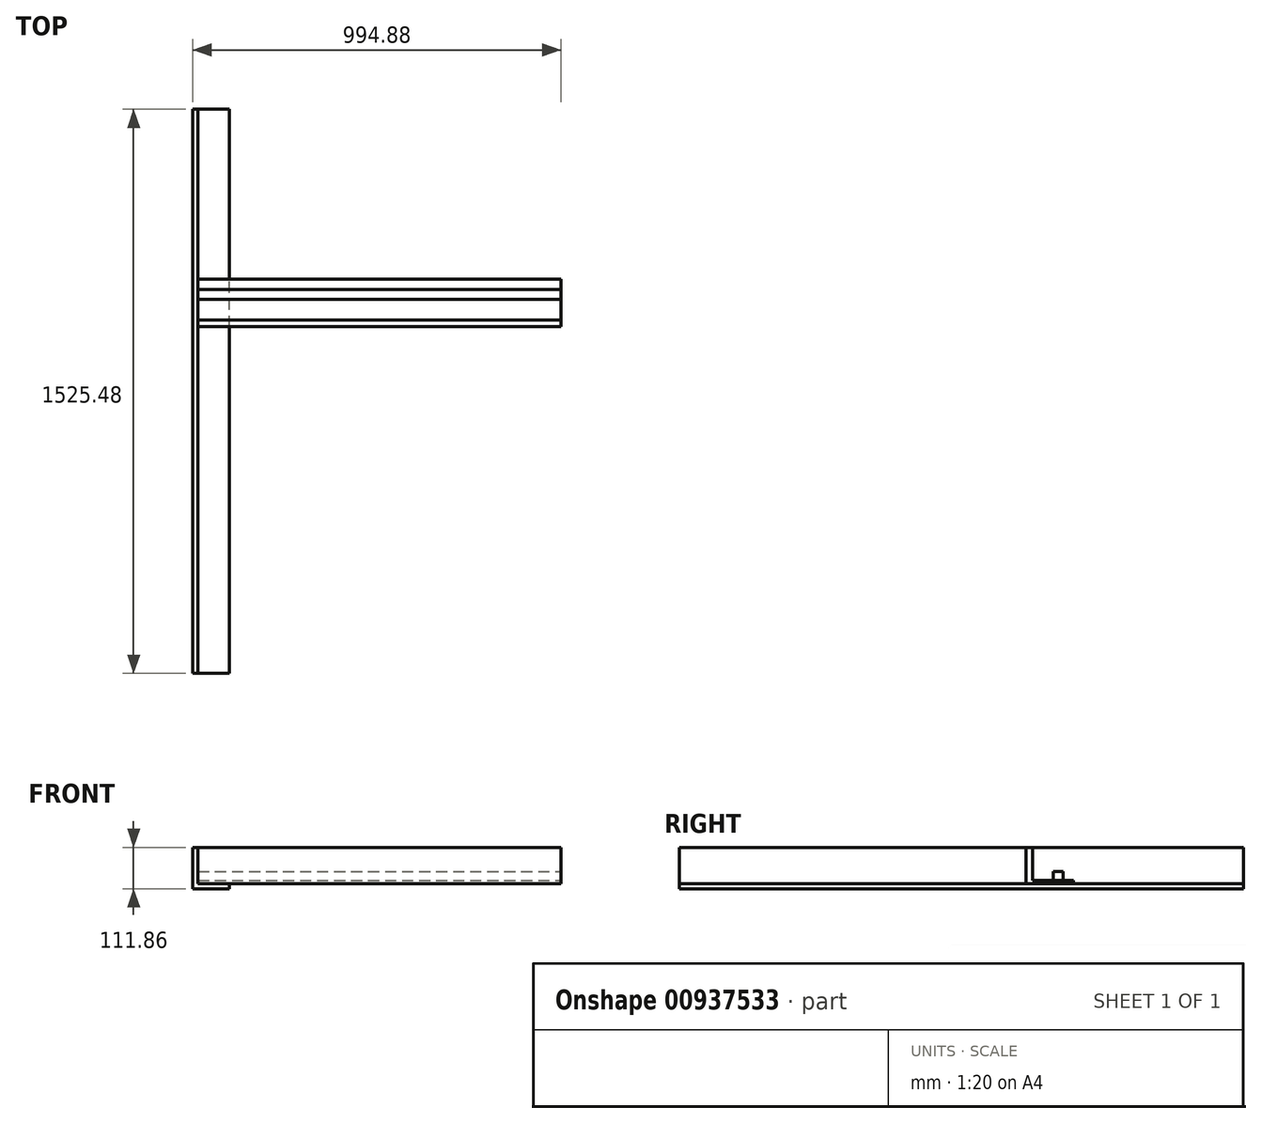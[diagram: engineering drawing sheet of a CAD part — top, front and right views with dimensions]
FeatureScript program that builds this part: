
annotation { "Feature Type Name" : "Feature", "Feature Type Description" : "" }
export const myFeature = defineFeature(function(context is Context, id is Id, definition is map)
    precondition{}
    {
        {
            var Q0;
            Q0=qCreatedBy(makeId("Front.planeOp"),FACE);
            var sketch = newSketch(context, id + "F0", { "sketchPlane" : qUnion([Q0])});
            skLineSegment(sketch, "E0", {"start": v(-31.08, 59.94) * mm, "end": v(-31.08, -51.92) * mm});
            skLineSegment(sketch, "E1", {"start": v(-31.08, -51.92) * mm, "end": v(67.23, -51.92) * mm});
            skLineSegment(sketch, "E2.0", {"start": v(-17.4, -38.23) * mm, "end": v(67.23, -38.23) * mm});
            skLineSegment(sketch, "E2.1", {"start": v(-17.4, 59.94) * mm, "end": v(-17.4, -38.23) * mm});
            skLineSegment(sketch, "E3", {"start": v(67.23, -51.92) * mm, "end": v(67.23, -23.4) * mm});
            skLineSegment(sketch, "E4", {"start": v(-32.97, 74.81) * mm, "end": v(-17.4, 59.94) * mm});
            skLineSegment(sketch, "E5", {"start": v(-33.22, 58.86) * mm, "end": v(-17.4, 59.94) * mm});
            skSolve(sketch);
        }
        {
            var Q0;
            {var subQ2=sQuery(id+"F0.wireOp",EDGE,"E1");Q0=makeQuery(id+"F0.imprint","IMPRINT",FACE,{"disambiguationData":[TD([[makeQuery(id+"F0.imprint","IMPRINT",EDGE,{"derivedFrom":subQ2}),1.0]])]});}
            extrude(context, id + "F1", {"entities" : qUnion([Q0]), "depth" : 1525.48 * mm, "offsetDistance" : 25 * mm});
        }
        {
            var Q0;
            Q0=makeQuery(id+"F1.opExtrude","SWEPT_FACE",FACE,{"disambiguationData":[OSD([sQuery(id+"F0.wireOp",EDGE,"E2.1")])]});
            var sketch = newSketch(context, id + "F2", { "sketchPlane" : qUnion([Q0])});
            skLineSegment(sketch, "E6", {"start": v(-588.2, 59.94) * mm, "end": v(-587.4, -38.23) * mm});
            skLineSegment(sketch, "E7", {"start": v(-459.17, -38.23) * mm, "end": v(-587.4, -38.23) * mm});
            skLineSegment(sketch, "E8.0", {"start": v(-588.44, 59.94) * mm, "end": v(-587.66, -38.23) * mm});
            skLineSegment(sketch, "E9", {"start": v(-588.2, 59.94) * mm, "end": v(-569.94, 59.94) * mm});
            skLineSegment(sketch, "E10", {"start": v(-569.94, 59.94) * mm, "end": v(-569.94, -29.83) * mm});
            skLineSegment(sketch, "E11", {"start": v(-569.94, -29.83) * mm, "end": v(-459.17, -29.83) * mm});
            skLineSegment(sketch, "E12", {"start": v(-459.17, -29.83) * mm, "end": v(-459.17, -38.23) * mm});
            skSolve(sketch);
        }
        {
            var Q0;
            Q0 = qSketchRegion(id + "F2", true);
            extrude(context, id + "F3", {"entities" : qUnion([Q0]), "depth" : 981.2 * mm, "offsetDistance" : 25 * mm});
        }
        {
            var Q0;
            Q0=makeQuery(id+"F3.opExtrude","SWEPT_FACE",FACE,{"disambiguationData":[OSD([sQuery(id+"F2.wireOp",EDGE,"E11")])]});
            var sketch = newSketch(context, id + "F4", { "sketchPlane" : qUnion([Q0])});
            skLineSegment(sketch, "E13.bottom", {"start": v(-17.4, -487.97) * mm, "end": v(963.8, -487.97) * mm});
            skLineSegment(sketch, "E13.top", {"start": v(-17.4, -514.56) * mm, "end": v(963.8, -514.56) * mm});
            skLineSegment(sketch, "E13.left", {"start": v(-17.4, -487.97) * mm, "end": v(-17.4, -514.56) * mm});
            skLineSegment(sketch, "E13.right", {"start": v(963.8, -487.97) * mm, "end": v(963.8, -514.56) * mm});
            skSolve(sketch);
        }
        {
            var Q0;
            Q0=makeQuery(id+"F4.imprint","IMPRINT",FACE,{"disambiguationData":[TD([[makeQuery(id+"F4.imprint","IMPRINT",EDGE,{"derivedFrom":sQuery(id+"F4.wireOp",EDGE,"E13.bottom")}),-1.0]])]});
            extrude(context, id + "F5", {"entities" : qUnion([Q0]), "depth" : 25 * mm, "offsetDistance" : 25 * mm});
        }
    });
